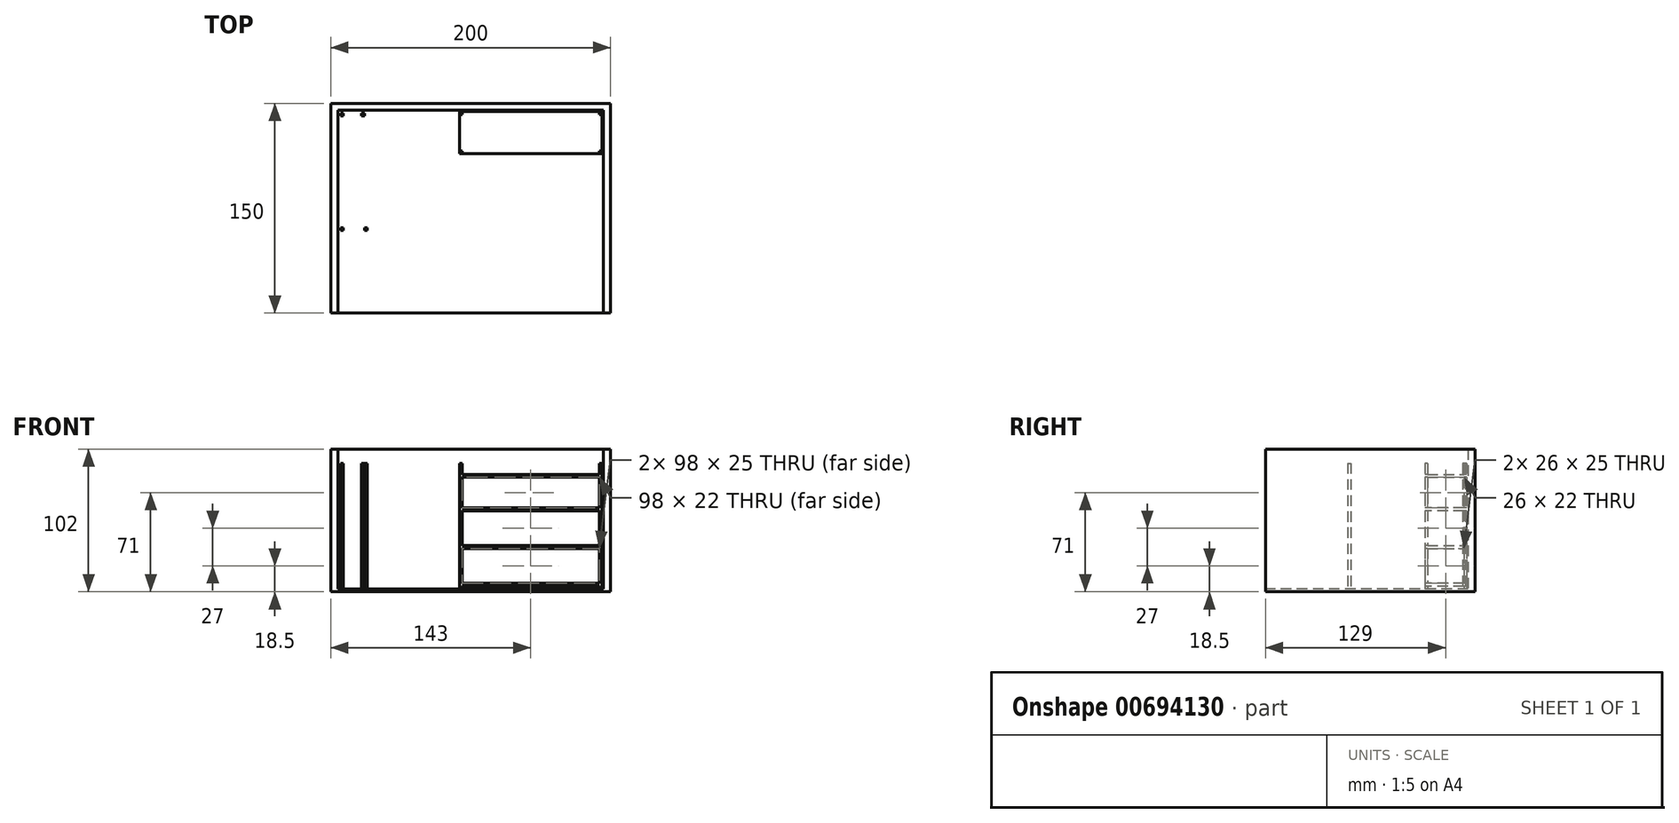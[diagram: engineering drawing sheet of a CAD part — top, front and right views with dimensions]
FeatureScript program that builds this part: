
annotation { "Feature Type Name" : "Feature", "Feature Type Description" : "" }
export const myFeature = defineFeature(function(context is Context, id is Id, definition is map)
    precondition{}
    {
        {
            var Q0;
            Q0=qCreatedBy(makeId("Top.planeOp"),FACE);
            var sketch = newSketch(context, id + "F0", { "sketchPlane" : qUnion([Q0])});
            skLineSegment(sketch, "E0.bottom", {"start": v(100, -75) * mm, "end": v(-100, -75) * mm});
            skLineSegment(sketch, "E0.top", {"start": v(100, 75) * mm, "end": v(-100, 75) * mm});
            skLineSegment(sketch, "E0.left", {"start": v(100, -75) * mm, "end": v(100, 75) * mm});
            skLineSegment(sketch, "E0.right", {"start": v(-100, -75) * mm, "end": v(-100, 75) * mm});
            skPoint(sketch, "E0.middle", {"position": v(0, 0) * mm});
            skSolve(sketch);
        }
        {
            var Q0;
            Q0=makeQuery(id+"F0.imprint","IMPRINT",FACE,{"disambiguationData":[TD([[makeQuery(id+"F0.imprint","IMPRINT",EDGE,{"derivedFrom":sQuery(id+"F0.wireOp",EDGE,"E0.bottom")}),-1.0]])]});
            extrude(context, id + "F1", {"entities" : qUnion([Q0]), "depth" : 2 * mm, "offsetDistance" : 25 * mm});
        }
        {
            var Q0;
            Q0=makeQuery(id+"F1.opExtrude","CAP_FACE",FACE,{"disambiguationData":[OSD([sQuery(id+"F0.wireOp",EDGE,"E0.bottom"),sQuery(id+"F0.wireOp",EDGE,"E0.top"),sQuery(id+"F0.wireOp",EDGE,"E0.left"),sQuery(id+"F0.wireOp",EDGE,"E0.right")])],"isStart":false});
            var sketch = newSketch(context, id + "F2", { "sketchPlane" : qUnion([Q0])});
            skLineSegment(sketch, "E1.bottom", {"start": v(-100, 75) * mm, "end": v(100, 75) * mm});
            skLineSegment(sketch, "E1.top", {"start": v(-100, 70) * mm, "end": v(100, 70) * mm});
            skLineSegment(sketch, "E1.left", {"start": v(-100, 75) * mm, "end": v(-100, 70) * mm});
            skLineSegment(sketch, "E1.right", {"start": v(100, 75) * mm, "end": v(100, 70) * mm});
            skLineSegment(sketch, "E2.bottom", {"start": v(-100, 75) * mm, "end": v(-95, 75) * mm});
            skLineSegment(sketch, "E2.top", {"start": v(-100, -75) * mm, "end": v(-95, -75) * mm});
            skLineSegment(sketch, "E2.left", {"start": v(-100, 75) * mm, "end": v(-100, -75) * mm});
            skLineSegment(sketch, "E2.right", {"start": v(-95, 75) * mm, "end": v(-95, -75) * mm});
            skLineSegment(sketch, "E3.bottom", {"start": v(100, 75) * mm, "end": v(95, 75) * mm});
            skLineSegment(sketch, "E3.top", {"start": v(100, -75) * mm, "end": v(95, -75) * mm});
            skLineSegment(sketch, "E3.left", {"start": v(100, 75) * mm, "end": v(100, -75) * mm});
            skLineSegment(sketch, "E3.right", {"start": v(95, 75) * mm, "end": v(95, -75) * mm});
            skSolve(sketch);
        }
        {
            var Q0;
            Q0 = qSketchRegion(id + "F2", true);
            extrude(context, id + "F3", {"entities" : qUnion([Q0]), "operationType" : NewBodyOperationType.ADD, "depth" : 100 * mm, "offsetDistance" : 25 * mm});
        }
        {
            var Q0;
            Q0=makeQuery(id+"F1.opExtrude","CAP_FACE",FACE,{"disambiguationData":[OSD([sQuery(id+"F0.wireOp",EDGE,"E0.bottom"),sQuery(id+"F0.wireOp",EDGE,"E0.top"),sQuery(id+"F0.wireOp",EDGE,"E0.left"),sQuery(id+"F0.wireOp",EDGE,"E0.right")])],"isStart":false});
            var sketch = newSketch(context, id + "F4", { "sketchPlane" : qUnion([Q0])});
            skLineSegment(sketch, "E4.bottom", {"start": v(94, 69) * mm, "end": v(92, 69) * mm});
            skLineSegment(sketch, "E4.top", {"start": v(94, 67) * mm, "end": v(92, 67) * mm});
            skLineSegment(sketch, "E4.left", {"start": v(94, 69) * mm, "end": v(94, 67) * mm});
            skLineSegment(sketch, "E4.right", {"start": v(92, 69) * mm, "end": v(92, 67) * mm});
            skLineSegment(sketch, "E5.1.0.0", {"start": v(-6, 69) * mm, "end": v(-8, 69) * mm});
            skLineSegment(sketch, "E5.1.0.1", {"start": v(-6, 69) * mm, "end": v(-6, 67) * mm});
            skLineSegment(sketch, "E5.1.0.2", {"start": v(-8, 69) * mm, "end": v(-8, 67) * mm});
            skLineSegment(sketch, "E5.1.0.3", {"start": v(-6, 67) * mm, "end": v(-8, 67) * mm});
            skLineSegment(sketch, "E6.bottom", {"start": v(-8, 41) * mm, "end": v(-6, 41) * mm});
            skLineSegment(sketch, "E6.top", {"start": v(-8, 39) * mm, "end": v(-6, 39) * mm});
            skLineSegment(sketch, "E6.left", {"start": v(-8, 41) * mm, "end": v(-8, 39) * mm});
            skLineSegment(sketch, "E6.right", {"start": v(-6, 41) * mm, "end": v(-6, 39) * mm});
            skLineSegment(sketch, "E7.bottom", {"start": v(92, 41) * mm, "end": v(94, 41) * mm});
            skLineSegment(sketch, "E7.top", {"start": v(92, 39) * mm, "end": v(94, 39) * mm});
            skLineSegment(sketch, "E7.left", {"start": v(92, 41) * mm, "end": v(92, 39) * mm});
            skLineSegment(sketch, "E7.right", {"start": v(94, 41) * mm, "end": v(94, 39) * mm});
            skLineSegment(sketch, "E8.bottom", {"start": v(-93, 68) * mm, "end": v(-91, 68) * mm});
            skLineSegment(sketch, "E8.top", {"start": v(-93, 66) * mm, "end": v(-91, 66) * mm});
            skLineSegment(sketch, "E8.left", {"start": v(-93, 68) * mm, "end": v(-93, 66) * mm});
            skLineSegment(sketch, "E8.right", {"start": v(-91, 68) * mm, "end": v(-91, 66) * mm});
            skLineSegment(sketch, "E9.bottom", {"start": v(-93, -16) * mm, "end": v(-91, -16) * mm});
            skLineSegment(sketch, "E9.top", {"start": v(-93, -14) * mm, "end": v(-91, -14) * mm});
            skLineSegment(sketch, "E9.left", {"start": v(-93, -16) * mm, "end": v(-93, -14) * mm});
            skLineSegment(sketch, "E9.right", {"start": v(-91, -16) * mm, "end": v(-91, -14) * mm});
            skLineSegment(sketch, "E10.bottom", {"start": v(-76, 68) * mm, "end": v(-78, 68) * mm});
            skLineSegment(sketch, "E10.top", {"start": v(-76, 66) * mm, "end": v(-78, 66) * mm});
            skLineSegment(sketch, "E10.left", {"start": v(-76, 68) * mm, "end": v(-76, 66) * mm});
            skLineSegment(sketch, "E10.right", {"start": v(-78, 68) * mm, "end": v(-78, 66) * mm});
            skLineSegment(sketch, "E11.bottom", {"start": v(-74, -14) * mm, "end": v(-76, -14) * mm});
            skLineSegment(sketch, "E11.top", {"start": v(-74, -16) * mm, "end": v(-76, -16) * mm});
            skLineSegment(sketch, "E11.left", {"start": v(-74, -14) * mm, "end": v(-74, -16) * mm});
            skLineSegment(sketch, "E11.right", {"start": v(-76, -14) * mm, "end": v(-76, -16) * mm});
            skLineSegment(sketch, "E12.0", {"start": v(-95, 70) * mm, "end": v(-95, -75) * mm});
            skLineSegment(sketch, "E13.0", {"start": v(-95, 70) * mm, "end": v(95, 70) * mm});
            skSolve(sketch);
        }
        {
            var Q0;
            Q0 = qSketchRegion(id + "F4", true);
            extrude(context, id + "F5", {"entities" : qUnion([Q0]), "operationType" : NewBodyOperationType.ADD, "depth" : 90 * mm, "offsetDistance" : 25 * mm});
        }
        {
            var Q0;
            Q0=makeQuery(id+"F5.opExtrude","CAP_FACE",FACE,{"disambiguationData":[OSD([sQuery(id+"F4.wireOp",EDGE,"E6.bottom"),sQuery(id+"F4.wireOp",EDGE,"E6.top"),sQuery(id+"F4.wireOp",EDGE,"E6.left"),sQuery(id+"F4.wireOp",EDGE,"E6.right")])],"isStart":false});
            cPlane(context, id + "F6", {"entities" : qUnion([Q0]), "cplaneType" : CPlaneType.OFFSET, "offset" : 10 * mm, "oppositeDirection" : true, "width" : 150 * mm, "height" : 150 * mm});
        }
        {
            var Q0;
            Q0=qCreatedBy(id+"F6.planeOp",FACE);
            var sketch = newSketch(context, id + "F7", { "sketchPlane" : qUnion([Q0])});
            skLineSegment(sketch, "E14.0.0", {"start": v(-8, 41) * mm, "end": v(-8, 39) * mm});
            skLineSegment(sketch, "E14.0.1", {"start": v(-8, 39) * mm, "end": v(-6, 39) * mm});
            skLineSegment(sketch, "E14.0.2", {"start": v(-6, 39) * mm, "end": v(-6, 41) * mm});
            skLineSegment(sketch, "E14.0.3", {"start": v(-6, 41) * mm, "end": v(-8, 41) * mm});
            skLineSegment(sketch, "E15.0.0", {"start": v(92, 67) * mm, "end": v(94, 67) * mm});
            skLineSegment(sketch, "E15.0.1", {"start": v(94, 67) * mm, "end": v(94, 69) * mm});
            skLineSegment(sketch, "E15.0.2", {"start": v(94, 69) * mm, "end": v(92, 69) * mm});
            skLineSegment(sketch, "E15.0.3", {"start": v(92, 69) * mm, "end": v(92, 67) * mm});
            skLineSegment(sketch, "E16.bottom", {"start": v(94, 69) * mm, "end": v(-8, 69) * mm});
            skLineSegment(sketch, "E16.top", {"start": v(94, 39) * mm, "end": v(-8, 39) * mm});
            skLineSegment(sketch, "E16.left", {"start": v(94, 69) * mm, "end": v(94, 39) * mm});
            skLineSegment(sketch, "E16.right", {"start": v(-8, 69) * mm, "end": v(-8, 39) * mm});
            skSolve(sketch);
        }
        {
            var Q0;
            Q0 = qSketchRegion(id + "F7", true);
            extrude(context, id + "F8", {"entities" : qUnion([Q0]), "operationType" : NewBodyOperationType.ADD, "depth" : 2 * mm, "offsetDistance" : 25 * mm});
        }
        {
            var Q0;
            Q0=makeQuery(id+"F8.opExtrude","CAP_FACE",FACE,{"disambiguationData":[OSD([sQuery(id+"F7.wireOp",EDGE,"E14.0.0"),sQuery(id+"F7.wireOp",EDGE,"E14.0.1"),sQuery(id+"F7.wireOp",EDGE,"E15.0.1"),sQuery(id+"F7.wireOp",EDGE,"E15.0.2"),sQuery(id+"F7.wireOp",EDGE,"E16.bottom"),sQuery(id+"F7.wireOp",EDGE,"E16.top"),sQuery(id+"F7.wireOp",EDGE,"E16.left"),sQuery(id+"F7.wireOp",EDGE,"E16.right")])],"isStart":false});
            cPlane(context, id + "F9", {"entities" : qUnion([Q0]), "cplaneType" : CPlaneType.OFFSET, "offset" : 80 * mm, "oppositeDirection" : true, "width" : 150 * mm, "height" : 150 * mm});
        }
        {
            var Q0;
            Q0=qCreatedBy(id+"F9.planeOp",FACE);
            var sketch = newSketch(context, id + "F10", { "sketchPlane" : qUnion([Q0])});
            skLineSegment(sketch, "E17.0.0", {"start": v(94, 41) * mm, "end": v(94, 67) * mm});
            skLineSegment(sketch, "E17.0.1", {"start": v(94, 67) * mm, "end": v(92, 67) * mm});
            skLineSegment(sketch, "E17.0.2", {"start": v(92, 67) * mm, "end": v(92, 69) * mm});
            skLineSegment(sketch, "E17.0.3", {"start": v(92, 69) * mm, "end": v(-6, 69) * mm});
            skLineSegment(sketch, "E17.0.4", {"start": v(-6, 69) * mm, "end": v(-6, 67) * mm});
            skLineSegment(sketch, "E17.0.5", {"start": v(-6, 67) * mm, "end": v(-8, 67) * mm});
            skLineSegment(sketch, "E17.0.6", {"start": v(-8, 67) * mm, "end": v(-8, 41) * mm});
            skLineSegment(sketch, "E17.0.7", {"start": v(-8, 41) * mm, "end": v(-6, 41) * mm});
            skLineSegment(sketch, "E17.0.8", {"start": v(-6, 41) * mm, "end": v(-6, 39) * mm});
            skLineSegment(sketch, "E17.0.9", {"start": v(-6, 39) * mm, "end": v(92, 39) * mm});
            skLineSegment(sketch, "E17.0.10", {"start": v(92, 39) * mm, "end": v(92, 41) * mm});
            skLineSegment(sketch, "E17.0.11", {"start": v(92, 41) * mm, "end": v(94, 41) * mm});
            skPoint(sketch, "E18.0", {"position": v(-8, 69) * mm});
            skPoint(sketch, "E19.0", {"position": v(94, 69) * mm});
            skPoint(sketch, "E20.0", {"position": v(94, 39) * mm});
            skPoint(sketch, "E21.0", {"position": v(-8, 39) * mm});
            skLineSegment(sketch, "E22.bottom", {"start": v(-8, 69) * mm, "end": v(94, 69) * mm});
            skLineSegment(sketch, "E22.top", {"start": v(-8, 39) * mm, "end": v(94, 39) * mm});
            skLineSegment(sketch, "E22.left", {"start": v(-8, 69) * mm, "end": v(-8, 39) * mm});
            skLineSegment(sketch, "E22.right", {"start": v(94, 69) * mm, "end": v(94, 39) * mm});
            skSolve(sketch);
        }
        {
            var Q0;
            Q0 = qSketchRegion(id + "F10", true);
            extrude(context, id + "F11", {"entities" : qUnion([Q0]), "operationType" : NewBodyOperationType.ADD, "depth" : 2 * mm, "offsetDistance" : 25 * mm});
        }
        {
            var Q0;
            Q0=makeQuery(id+"F11.opExtrude","CAP_FACE",FACE,{"disambiguationData":[OSD([sQuery(id+"F10.wireOp",EDGE,"E17.0.0"),sQuery(id+"F10.wireOp",EDGE,"E17.0.3"),sQuery(id+"F10.wireOp",EDGE,"E17.0.6"),sQuery(id+"F10.wireOp",EDGE,"E17.0.9"),sQuery(id+"F10.wireOp",EDGE,"E22.bottom"),sQuery(id+"F10.wireOp",EDGE,"E22.top"),sQuery(id+"F10.wireOp",EDGE,"E22.left"),sQuery(id+"F10.wireOp",EDGE,"E22.right")])],"isStart":false});
            cPlane(context, id + "F12", {"entities" : qUnion([Q0]), "cplaneType" : CPlaneType.OFFSET, "offset" : 25 * mm, "width" : 150 * mm, "height" : 150 * mm});
        }
        {
            var Q0;
            Q0=qCreatedBy(id+"F12.planeOp",FACE);
            var sketch = newSketch(context, id + "F13", { "sketchPlane" : qUnion([Q0])});
            skLineSegment(sketch, "E23.0.0", {"start": v(94, 41) * mm, "end": v(94, 67) * mm});
            skLineSegment(sketch, "E23.0.1", {"start": v(94, 67) * mm, "end": v(92, 67) * mm});
            skLineSegment(sketch, "E23.0.2", {"start": v(92, 67) * mm, "end": v(92, 69) * mm});
            skLineSegment(sketch, "E23.0.3", {"start": v(92, 69) * mm, "end": v(-6, 69) * mm});
            skLineSegment(sketch, "E23.0.4", {"start": v(-6, 69) * mm, "end": v(-6, 67) * mm});
            skLineSegment(sketch, "E23.0.5", {"start": v(-6, 67) * mm, "end": v(-8, 67) * mm});
            skLineSegment(sketch, "E23.0.6", {"start": v(-8, 67) * mm, "end": v(-8, 41) * mm});
            skLineSegment(sketch, "E23.0.7", {"start": v(-8, 41) * mm, "end": v(-6, 41) * mm});
            skLineSegment(sketch, "E23.0.8", {"start": v(-6, 41) * mm, "end": v(-6, 39) * mm});
            skLineSegment(sketch, "E23.0.9", {"start": v(-6, 39) * mm, "end": v(92, 39) * mm});
            skLineSegment(sketch, "E23.0.10", {"start": v(92, 39) * mm, "end": v(92, 41) * mm});
            skLineSegment(sketch, "E23.0.11", {"start": v(92, 41) * mm, "end": v(94, 41) * mm});
            skPoint(sketch, "E24.0", {"position": v(-8, 69) * mm});
            skPoint(sketch, "E25.0", {"position": v(-8, 39) * mm});
            skPoint(sketch, "E26.0", {"position": v(94, 39) * mm});
            skPoint(sketch, "E27.0", {"position": v(94, 69) * mm});
            skLineSegment(sketch, "E28.bottom", {"start": v(-8, 39) * mm, "end": v(94, 39) * mm});
            skLineSegment(sketch, "E28.top", {"start": v(-8, 69) * mm, "end": v(94, 69) * mm});
            skLineSegment(sketch, "E28.left", {"start": v(-8, 39) * mm, "end": v(-8, 69) * mm});
            skLineSegment(sketch, "E28.right", {"start": v(94, 39) * mm, "end": v(94, 69) * mm});
            skSolve(sketch);
        }
        {
            var Q0;
            Q0 = qSketchRegion(id + "F13", true);
            extrude(context, id + "F14", {"entities" : qUnion([Q0]), "operationType" : NewBodyOperationType.ADD, "depth" : 2 * mm, "offsetDistance" : 25 * mm});
        }
        {
            var Q0;
            Q0=makeQuery(id+"F14.opExtrude","CAP_FACE",FACE,{"disambiguationData":[OSD([sQuery(id+"F13.wireOp",EDGE,"E23.0.0"),sQuery(id+"F13.wireOp",EDGE,"E23.0.3"),sQuery(id+"F13.wireOp",EDGE,"E23.0.6"),sQuery(id+"F13.wireOp",EDGE,"E23.0.9"),sQuery(id+"F13.wireOp",EDGE,"E28.bottom"),sQuery(id+"F13.wireOp",EDGE,"E28.top"),sQuery(id+"F13.wireOp",EDGE,"E28.left"),sQuery(id+"F13.wireOp",EDGE,"E28.right")])],"isStart":false});
            cPlane(context, id + "F15", {"entities" : qUnion([Q0]), "cplaneType" : CPlaneType.OFFSET, "offset" : 25 * mm, "width" : 150 * mm, "height" : 150 * mm});
        }
        {
            var Q0;
            Q0=qCreatedBy(id+"F15.planeOp",FACE);
            var sketch = newSketch(context, id + "F16", { "sketchPlane" : qUnion([Q0])});
            skPoint(sketch, "E29.0", {"position": v(-8, 69) * mm});
            skPoint(sketch, "E30.0", {"position": v(-8, 39) * mm});
            skPoint(sketch, "E31.0", {"position": v(94, 39) * mm});
            skPoint(sketch, "E32.0", {"position": v(94, 69) * mm});
            skLineSegment(sketch, "E33.bottom", {"start": v(-8, 69) * mm, "end": v(94, 69) * mm});
            skLineSegment(sketch, "E33.top", {"start": v(-8, 39) * mm, "end": v(94, 39) * mm});
            skLineSegment(sketch, "E33.left", {"start": v(-8, 69) * mm, "end": v(-8, 39) * mm});
            skLineSegment(sketch, "E33.right", {"start": v(94, 69) * mm, "end": v(94, 39) * mm});
            skSolve(sketch);
        }
        {
            var Q0;
            Q0 = qSketchRegion(id + "F16", true);
            extrude(context, id + "F17", {"entities" : qUnion([Q0]), "operationType" : NewBodyOperationType.ADD, "depth" : 2 * mm, "offsetDistance" : 25 * mm});
        }
    });
